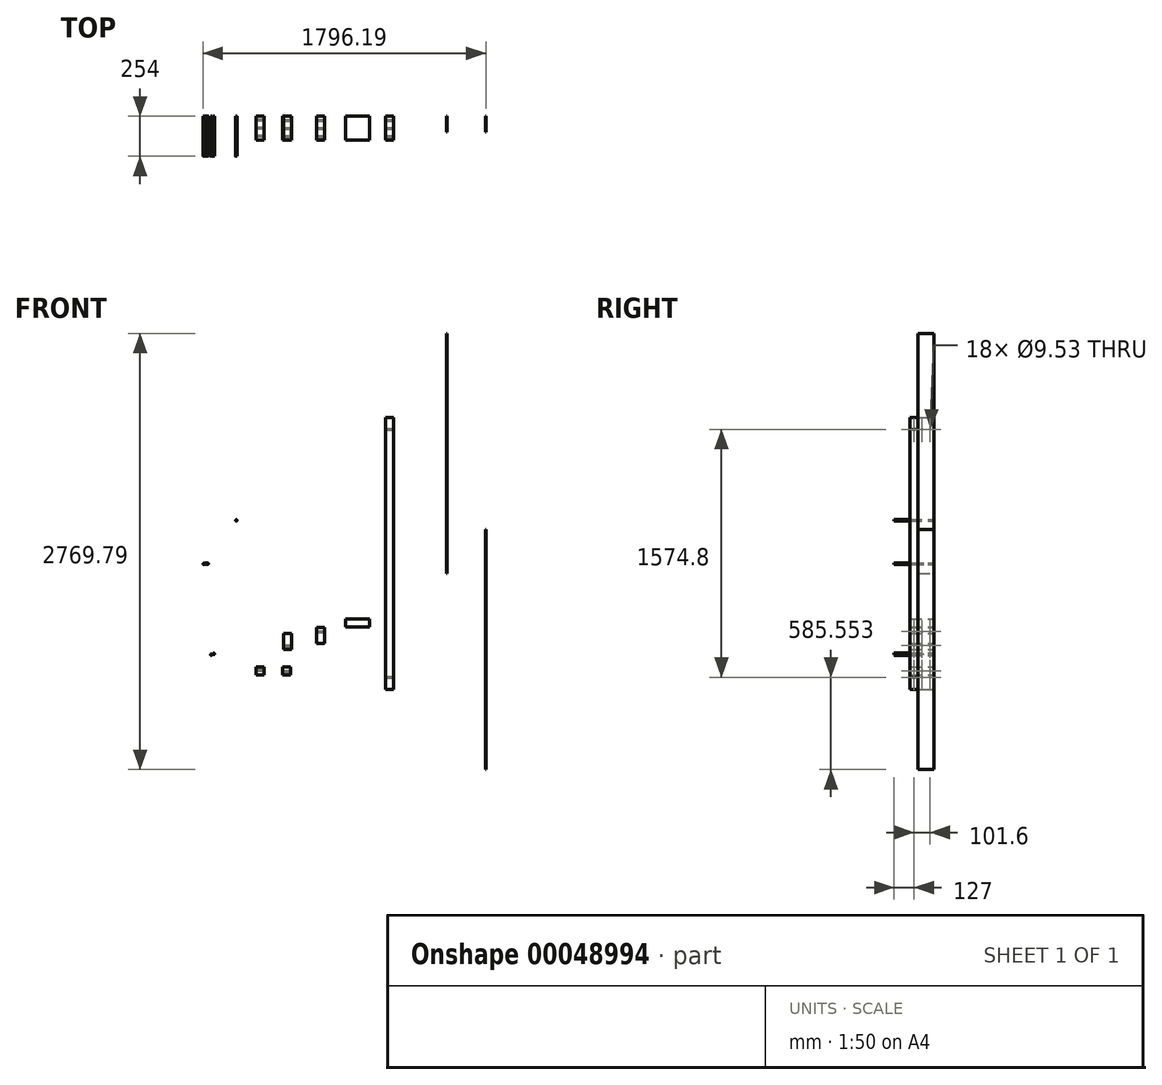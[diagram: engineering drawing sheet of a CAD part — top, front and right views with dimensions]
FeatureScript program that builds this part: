
annotation { "Feature Type Name" : "Feature", "Feature Type Description" : "" }
export const myFeature = defineFeature(function(context is Context, id is Id, definition is map)
    precondition{}
    {
        {
            var Q0;
            Q0=qCreatedBy(makeId("Front.planeOp"),FACE);
            var sketch = newSketch(context, id + "F0", { "sketchPlane" : qUnion([Q0])});
            skLineSegment(sketch, "E0.bottom", {"start": v(-472.01, 118.29) * mm, "end": v(-421.21, 118.29) * mm});
            skLineSegment(sketch, "E0.top", {"start": v(-472.01, 16.69) * mm, "end": v(-421.21, 16.69) * mm});
            skLineSegment(sketch, "E0.left", {"start": v(-472.01, 118.29) * mm, "end": v(-472.01, 16.69) * mm});
            skLineSegment(sketch, "E0.right", {"start": v(-421.21, 118.29) * mm, "end": v(-421.21, 16.69) * mm});
            skLineSegment(sketch, "E1.top", {"start": v(-262.5, 54) * mm, "end": v(-211.7, 54) * mm});
            skLineSegment(sketch, "E1.left", {"start": v(-262.5, 155.6) * mm, "end": v(-262.5, 54) * mm});
            skLineSegment(sketch, "E1.right", {"start": v(-211.7, 155.6) * mm, "end": v(-211.7, 54) * mm});
            skLineSegment(sketch, "E1.bottom", {"start": v(-262.5, 155.6) * mm, "end": v(-211.7, 155.6) * mm});
            skLineSegment(sketch, "E2.bottom", {"start": v(-645.87, -93.88) * mm, "end": v(-595.07, -93.88) * mm});
            skLineSegment(sketch, "E2.top", {"start": v(-645.87, -144.68) * mm, "end": v(-595.07, -144.68) * mm});
            skLineSegment(sketch, "E2.left", {"start": v(-645.87, -93.88) * mm, "end": v(-645.87, -144.68) * mm});
            skLineSegment(sketch, "E2.right", {"start": v(-595.07, -93.88) * mm, "end": v(-595.07, -144.68) * mm});
            skLineSegment(sketch, "E3.bottom", {"start": v(-479.26, -94.3) * mm, "end": v(-428.46, -94.3) * mm});
            skLineSegment(sketch, "E3.top", {"start": v(-479.26, -145.1) * mm, "end": v(-428.46, -145.1) * mm});
            skLineSegment(sketch, "E3.left", {"start": v(-479.26, -94.3) * mm, "end": v(-479.26, -145.1) * mm});
            skLineSegment(sketch, "E3.right", {"start": v(-428.46, -94.3) * mm, "end": v(-428.46, -145.1) * mm});
            skLineSegment(sketch, "E4.bottom", {"start": v(-77.8, 209.71) * mm, "end": v(74.6, 209.71) * mm});
            skLineSegment(sketch, "E4.top", {"start": v(-77.8, 158.91) * mm, "end": v(74.6, 158.91) * mm});
            skLineSegment(sketch, "E4.left", {"start": v(-77.8, 209.71) * mm, "end": v(-77.8, 158.91) * mm});
            skLineSegment(sketch, "E4.right", {"start": v(74.6, 209.71) * mm, "end": v(74.6, 158.91) * mm});
            skLineSegment(sketch, "E5.bottom", {"start": v(177.1, 1490.91) * mm, "end": v(227.9, 1490.91) * mm});
            skLineSegment(sketch, "E5.top", {"start": v(177.1, -236.29) * mm, "end": v(227.9, -236.29) * mm});
            skLineSegment(sketch, "E5.left", {"start": v(177.1, 1490.91) * mm, "end": v(177.1, -236.29) * mm});
            skLineSegment(sketch, "E5.right", {"start": v(227.9, 1490.91) * mm, "end": v(227.9, -236.29) * mm});
            skSolve(sketch);
        }
        {
            var Q0;
            Q0=makeQuery(id+"F0.imprint","IMPRINT",FACE,{"disambiguationData":[TD([[makeQuery(id+"F0.imprint","IMPRINT",EDGE,{"derivedFrom":sQuery(id+"F0.wireOp",EDGE,"E0.bottom")}),-1.0]])]});
            extrude(context, id + "F1", {"entities" : qUnion([Q0]), "depth" : 152.4 * mm});
        }
        {
            var Q0;
            Q0=makeQuery(id+"F0.imprint","IMPRINT",FACE,{"disambiguationData":[TD([[makeQuery(id+"F0.imprint","IMPRINT",EDGE,{"derivedFrom":sQuery(id+"F0.wireOp",EDGE,"E1.top")}),1.0]])]});
            extrude(context, id + "F2", {"entities" : qUnion([Q0]), "depth" : 152.4 * mm});
        }
        {
            var Q0;
            Q0=makeQuery(id+"F0.imprint","IMPRINT",FACE,{"disambiguationData":[TD([[makeQuery(id+"F0.imprint","IMPRINT",EDGE,{"derivedFrom":sQuery(id+"F0.wireOp",EDGE,"E4.bottom")}),-1.0]])]});
            extrude(context, id + "F3", {"entities" : qUnion([Q0]), "depth" : 152.4 * mm});
        }
        {
            var Q0;
            Q0=makeQuery(id+"F0.imprint","IMPRINT",FACE,{"disambiguationData":[TD([[makeQuery(id+"F0.imprint","IMPRINT",EDGE,{"derivedFrom":sQuery(id+"F0.wireOp",EDGE,"E2.bottom")}),-1.0]])]});
            var Q1;
            Q1=makeQuery(id+"F0.imprint","IMPRINT",FACE,{"disambiguationData":[TD([[makeQuery(id+"F0.imprint","IMPRINT",EDGE,{"derivedFrom":sQuery(id+"F0.wireOp",EDGE,"E3.bottom")}),-1.0]])]});
            var Q2;
            Q2=makeQuery(id+"F0.imprint","IMPRINT",FACE,{"disambiguationData":[TD([[makeQuery(id+"F0.imprint","IMPRINT",EDGE,{"derivedFrom":sQuery(id+"F0.wireOp",EDGE,"E5.bottom")}),-1.0]])]});
            extrude(context, id + "F4", {"entities" : qUnion([Q0, Q1, Q2]), "depth" : 152.4 * mm});
        }
        {
            var Q0;
            Q0=qCreatedBy(makeId("Front.planeOp"),FACE);
            var sketch = newSketch(context, id + "F5", { "sketchPlane" : qUnion([Q0])});
            skLineSegment(sketch, "E6.bottom", {"start": v(563.4, 2024.15) * mm, "end": v(566.58, 2024.15) * mm});
            skLineSegment(sketch, "E6.top", {"start": v(563.4, 500.15) * mm, "end": v(566.58, 500.15) * mm});
            skLineSegment(sketch, "E6.left", {"start": v(563.4, 2024.15) * mm, "end": v(563.4, 500.15) * mm});
            skLineSegment(sketch, "E6.right", {"start": v(566.58, 2024.15) * mm, "end": v(566.58, 500.15) * mm});
            skLineSegment(sketch, "E7.right", {"start": v(813.62, 778.36) * mm, "end": v(813.62, -745.64) * mm});
            skLineSegment(sketch, "E7.left", {"start": v(810.45, 778.36) * mm, "end": v(810.45, -745.64) * mm});
            skLineSegment(sketch, "E7.top", {"start": v(810.45, -745.64) * mm, "end": v(813.62, -745.64) * mm});
            skLineSegment(sketch, "E7.bottom", {"start": v(810.45, 778.36) * mm, "end": v(813.62, 778.36) * mm});
            skSolve(sketch);
        }
        {
            var Q0;
            Q0=makeQuery(id+"F5.imprint","IMPRINT",FACE,{"disambiguationData":[TD([[makeQuery(id+"F5.imprint","IMPRINT",EDGE,{"derivedFrom":sQuery(id+"F5.wireOp",EDGE,"E6.bottom")}),-1.0]])]});
            var Q1;
            Q1=makeQuery(id+"F5.imprint","IMPRINT",FACE,{"disambiguationData":[TD([[makeQuery(id+"F5.imprint","IMPRINT",EDGE,{"derivedFrom":sQuery(id+"F5.wireOp",EDGE,"E7.right")}),-1.0]])]});
            extrude(context, id + "F6", {"entities" : qUnion([Q0, Q1]), "depth" : 101.6 * mm});
        }
        {
            var Q0;
            Q0=qCreatedBy(makeId("Front.planeOp"),FACE);
            var sketch = newSketch(context, id + "F7", { "sketchPlane" : qUnion([Q0])});
            skCircle(sketch, "E8", {"center": v(-772.5, 836.22) * mm, "radius": 4.76 * mm});
            skSolve(sketch);
        }
        {
            var Q0;
            Q0=makeQuery(id+"F7.imprint","IMPRINT",FACE,{"disambiguationData":[TD([[makeQuery(id+"F7.imprint","IMPRINT",EDGE,{"derivedFrom":sQuery(id+"F7.wireOp",EDGE,"E8")}),1.0]])]});
            extrude(context, id + "F8", {"entities" : qUnion([Q0]), "depth" : 254 * mm});
        }
        {
            var Q0;
            Q0=qCreatedBy(makeId("Front.planeOp"),FACE);
            var sketch = newSketch(context, id + "F9", { "sketchPlane" : qUnion([Q0])});
            skCircle(sketch, "E9", {"center": v(-931.08, -16.23) * mm, "radius": 4.76 * mm});
            skSolve(sketch);
        }
        {
            var Q0;
            Q0=qCreatedBy(makeId("Front.planeOp"),FACE);
            var sketch = newSketch(context, id + "F10", { "sketchPlane" : qUnion([Q0])});
            skCircle(sketch, "E10", {"center": v(-915.13, -11.65) * mm, "radius": 4.76 * mm});
            skSolve(sketch);
        }
        {
            var Q0;
            Q0=makeQuery(id+"F9.imprint","IMPRINT",FACE,{"disambiguationData":[TD([[makeQuery(id+"F9.imprint","IMPRINT",EDGE,{"derivedFrom":sQuery(id+"F9.wireOp",EDGE,"E9")}),1.0]])]});
            var Q1;
            Q1=makeQuery(id+"F10.imprint","IMPRINT",FACE,{"disambiguationData":[TD([[makeQuery(id+"F10.imprint","IMPRINT",EDGE,{"derivedFrom":sQuery(id+"F10.wireOp",EDGE,"E10")}),1.0]])]});
            extrude(context, id + "F11", {"entities" : qUnion([Q0, Q1]), "depth" : 254 * mm});
        }
        {
            var Q0;
            Q0=makeQuery(id+"F4.opExtrude","SWEPT_FACE",FACE,{"disambiguationData":[OSD([sQuery(id+"F0.wireOp",EDGE,"E2.left")])]});
            var sketch = newSketch(context, id + "F12", { "sketchPlane" : qUnion([Q0])});
            skLineSegment(sketch, "E11.bottom", {"start": v(152.4, -93.88) * mm, "end": v(127, -93.88) * mm});
            skLineSegment(sketch, "E11.top", {"start": v(152.4, -119.28) * mm, "end": v(127, -119.28) * mm});
            skLineSegment(sketch, "E11.left", {"start": v(152.4, -93.88) * mm, "end": v(152.4, -119.28) * mm});
            skLineSegment(sketch, "E11.right", {"start": v(127, -93.88) * mm, "end": v(127, -119.28) * mm});
            skLineSegment(sketch, "E12.bottom", {"start": v(0, -93.88) * mm, "end": v(25.4, -93.88) * mm});
            skLineSegment(sketch, "E12.top", {"start": v(0, -119.28) * mm, "end": v(25.4, -119.28) * mm});
            skLineSegment(sketch, "E12.left", {"start": v(0, -93.88) * mm, "end": v(0, -119.28) * mm});
            skLineSegment(sketch, "E12.right", {"start": v(25.4, -93.88) * mm, "end": v(25.4, -119.28) * mm});
            skLineSegment(sketch, "E13.bottom", {"start": v(0, -93.88) * mm, "end": v(76.2, -93.88) * mm});
            skLineSegment(sketch, "E13.top", {"start": v(0, -119.28) * mm, "end": v(76.2, -119.28) * mm});
            skLineSegment(sketch, "E13.right", {"start": v(76.2, -93.88) * mm, "end": v(76.2, -119.28) * mm});
            skSolve(sketch);
        }
        {
            var Q0;
            Q0=sQuery(id+"F12.wireOp",VERTEX,"E12.top.end");
            var Q1;
            Q1=sQuery(id+"F12.wireOp",VERTEX,"E11.right.end");
            var Q2;
            Q2=sQuery(id+"F12.wireOp",VERTEX,"E13.top.end");
            var Q3;
            Q3=makeQuery(id+"F4.opExtrude","SWEPT_BODY",BODY,{"disambiguationData":[OSD([sQuery(id+"F0.wireOp",EDGE,"E2.bottom"),sQuery(id+"F0.wireOp",EDGE,"E2.top"),sQuery(id+"F0.wireOp",EDGE,"E2.left"),sQuery(id+"F0.wireOp",EDGE,"E2.right")])]});
            hole(context, id + "F13", {"style" : HoleStyle.SIMPLE, "holeDiameter" : 9.52 * mm, "endStyle" : HoleEndStyle.THROUGH, "locations" : qUnion([Q0, Q1, Q2]), "scope" : qUnion([Q3])});
        }
        {
            var Q0;
            Q0=makeQuery(id+"F4.opExtrude","SWEPT_FACE",FACE,{"disambiguationData":[OSD([sQuery(id+"F0.wireOp",EDGE,"E3.right")])]});
            var sketch = newSketch(context, id + "F14", { "sketchPlane" : qUnion([Q0])});
            skLineSegment(sketch, "E14.bottom", {"start": v(-152.4, -94.3) * mm, "end": v(-127, -94.3) * mm});
            skLineSegment(sketch, "E14.top", {"start": v(-152.4, -119.7) * mm, "end": v(-127, -119.7) * mm});
            skLineSegment(sketch, "E14.left", {"start": v(-152.4, -94.3) * mm, "end": v(-152.4, -119.7) * mm});
            skLineSegment(sketch, "E14.right", {"start": v(-127, -94.3) * mm, "end": v(-127, -119.7) * mm});
            skLineSegment(sketch, "E15.bottom", {"start": v(0, -94.3) * mm, "end": v(-25.4, -94.3) * mm});
            skLineSegment(sketch, "E15.top", {"start": v(0, -119.7) * mm, "end": v(-25.4, -119.7) * mm});
            skLineSegment(sketch, "E15.left", {"start": v(0, -94.3) * mm, "end": v(0, -119.7) * mm});
            skLineSegment(sketch, "E15.right", {"start": v(-25.4, -94.3) * mm, "end": v(-25.4, -119.7) * mm});
            skLineSegment(sketch, "E16.bottom", {"start": v(0, -145.1) * mm, "end": v(-76.2, -145.1) * mm});
            skLineSegment(sketch, "E16.top", {"start": v(0, -119.7) * mm, "end": v(-76.2, -119.7) * mm});
            skLineSegment(sketch, "E16.left", {"start": v(0, -145.1) * mm, "end": v(0, -119.7) * mm});
            skLineSegment(sketch, "E16.right", {"start": v(-76.2, -145.1) * mm, "end": v(-76.2, -119.7) * mm});
            skSolve(sketch);
        }
        {
            var Q0;
            Q0=sQuery(id+"F14.wireOp",VERTEX,"E14.top.end");
            var Q1;
            Q1=sQuery(id+"F14.wireOp",VERTEX,"E16.right.end");
            var Q2;
            Q2=sQuery(id+"F14.wireOp",VERTEX,"E15.right.end");
            var Q3;
            Q3=makeQuery(id+"F4.opExtrude","SWEPT_BODY",BODY,{"disambiguationData":[OSD([sQuery(id+"F0.wireOp",EDGE,"E3.bottom"),sQuery(id+"F0.wireOp",EDGE,"E3.top"),sQuery(id+"F0.wireOp",EDGE,"E3.left"),sQuery(id+"F0.wireOp",EDGE,"E3.right")])]});
            hole(context, id + "F15", {"style" : HoleStyle.SIMPLE, "holeDiameter" : 9.52 * mm, "endStyle" : HoleEndStyle.THROUGH, "locations" : qUnion([Q0, Q1, Q2]), "scope" : qUnion([Q3])});
        }
        {
            var Q0;
            Q0=makeQuery(id+"F1.opExtrude","SWEPT_FACE",FACE,{"disambiguationData":[OSD([sQuery(id+"F0.wireOp",EDGE,"E0.right")])]});
            var sketch = newSketch(context, id + "F16", { "sketchPlane" : qUnion([Q0])});
            skLineSegment(sketch, "E17.bottom", {"start": v(-152.4, 16.69) * mm, "end": v(-127, 16.69) * mm});
            skLineSegment(sketch, "E17.top", {"start": v(-152.4, 42.09) * mm, "end": v(-127, 42.09) * mm});
            skLineSegment(sketch, "E17.left", {"start": v(-152.4, 16.69) * mm, "end": v(-152.4, 42.09) * mm});
            skLineSegment(sketch, "E17.right", {"start": v(-127, 16.69) * mm, "end": v(-127, 42.09) * mm});
            skLineSegment(sketch, "E18.bottom", {"start": v(0, 16.69) * mm, "end": v(-25.4, 16.69) * mm});
            skLineSegment(sketch, "E18.top", {"start": v(0, 42.09) * mm, "end": v(-25.4, 42.09) * mm});
            skLineSegment(sketch, "E18.left", {"start": v(0, 16.69) * mm, "end": v(0, 42.09) * mm});
            skLineSegment(sketch, "E18.right", {"start": v(-25.4, 16.69) * mm, "end": v(-25.4, 42.09) * mm});
            skLineSegment(sketch, "E19.bottom", {"start": v(0, 16.69) * mm, "end": v(-76.2, 16.69) * mm});
            skLineSegment(sketch, "E19.top", {"start": v(0, 42.09) * mm, "end": v(-76.2, 42.09) * mm});
            skLineSegment(sketch, "E19.right", {"start": v(-76.2, 16.69) * mm, "end": v(-76.2, 42.09) * mm});
            skSolve(sketch);
        }
        {
            var Q0;
            Q0=sQuery(id+"F16.wireOp",VERTEX,"E17.right.end");
            var Q1;
            Q1=sQuery(id+"F16.wireOp",VERTEX,"E19.top.end");
            var Q2;
            Q2=sQuery(id+"F16.wireOp",VERTEX,"E18.right.end");
            var Q3;
            Q3=makeQuery(id+"F1.opExtrude","SWEPT_BODY",BODY,{"disambiguationData":[OSD([sQuery(id+"F0.wireOp",EDGE,"E0.bottom"),sQuery(id+"F0.wireOp",EDGE,"E0.top"),sQuery(id+"F0.wireOp",EDGE,"E0.left"),sQuery(id+"F0.wireOp",EDGE,"E0.right")])]});
            hole(context, id + "F17", {"style" : HoleStyle.SIMPLE, "holeDiameter" : 9.52 * mm, "endStyle" : HoleEndStyle.THROUGH, "locations" : qUnion([Q0, Q1, Q2]), "scope" : qUnion([Q3])});
        }
        {
            var Q0;
            Q0=makeQuery(id+"F2.opExtrude","SWEPT_FACE",FACE,{"disambiguationData":[OSD([sQuery(id+"F0.wireOp",EDGE,"E1.right")])]});
            var sketch = newSketch(context, id + "F18", { "sketchPlane" : qUnion([Q0])});
            skLineSegment(sketch, "E20.bottom", {"start": v(-152.4, 54) * mm, "end": v(-127, 54) * mm});
            skLineSegment(sketch, "E20.top", {"start": v(-152.4, 130.2) * mm, "end": v(-127, 130.2) * mm});
            skLineSegment(sketch, "E20.left", {"start": v(-152.4, 54) * mm, "end": v(-152.4, 130.2) * mm});
            skLineSegment(sketch, "E20.right", {"start": v(-127, 54) * mm, "end": v(-127, 130.2) * mm});
            skLineSegment(sketch, "E21.bottom", {"start": v(-152.4, 54) * mm, "end": v(-76.2, 54) * mm});
            skLineSegment(sketch, "E21.top", {"start": v(-152.4, 130.2) * mm, "end": v(-76.2, 130.2) * mm});
            skLineSegment(sketch, "E21.right", {"start": v(-76.2, 54) * mm, "end": v(-76.2, 130.2) * mm});
            skLineSegment(sketch, "E22.bottom", {"start": v(0, 54) * mm, "end": v(-25.4, 54) * mm});
            skLineSegment(sketch, "E22.top", {"start": v(0, 130.2) * mm, "end": v(-25.4, 130.2) * mm});
            skLineSegment(sketch, "E22.left", {"start": v(0, 54) * mm, "end": v(0, 130.2) * mm});
            skLineSegment(sketch, "E22.right", {"start": v(-25.4, 54) * mm, "end": v(-25.4, 130.2) * mm});
            skSolve(sketch);
        }
        {
            var Q0;
            Q0=sQuery(id+"F18.wireOp",VERTEX,"E20.right.end");
            var Q1;
            Q1=sQuery(id+"F18.wireOp",VERTEX,"E21.top.end");
            var Q2;
            Q2=sQuery(id+"F18.wireOp",VERTEX,"E22.right.end");
            var Q3;
            Q3=makeQuery(id+"F2.opExtrude","SWEPT_BODY",BODY,{"disambiguationData":[OSD([sQuery(id+"F0.wireOp",EDGE,"E1.top"),sQuery(id+"F0.wireOp",EDGE,"E1.left"),sQuery(id+"F0.wireOp",EDGE,"E1.right"),sQuery(id+"F0.wireOp",EDGE,"E1.bottom")])]});
            hole(context, id + "F19", {"style" : HoleStyle.SIMPLE, "holeDiameter" : 9.52 * mm, "endStyle" : HoleEndStyle.THROUGH, "locations" : qUnion([Q0, Q1, Q2]), "scope" : qUnion([Q3])});
        }
        {
            var Q0;
            Q0=makeQuery(id+"F4.opExtrude","SWEPT_FACE",FACE,{"disambiguationData":[OSD([sQuery(id+"F0.wireOp",EDGE,"E5.right")])]});
            var sketch = newSketch(context, id + "F20", { "sketchPlane" : qUnion([Q0])});
            skLineSegment(sketch, "E23.bottom", {"start": v(-152.4, 1490.91) * mm, "end": v(-127, 1490.91) * mm});
            skLineSegment(sketch, "E23.top", {"start": v(-152.4, 1414.71) * mm, "end": v(-127, 1414.71) * mm});
            skLineSegment(sketch, "E23.left", {"start": v(-152.4, 1490.91) * mm, "end": v(-152.4, 1414.71) * mm});
            skLineSegment(sketch, "E23.right", {"start": v(-127, 1490.91) * mm, "end": v(-127, 1414.71) * mm});
            skLineSegment(sketch, "E24.bottom", {"start": v(-152.4, 1490.91) * mm, "end": v(-76.2, 1490.91) * mm});
            skLineSegment(sketch, "E24.top", {"start": v(-152.4, 1414.71) * mm, "end": v(-76.2, 1414.71) * mm});
            skLineSegment(sketch, "E24.right", {"start": v(-76.2, 1490.91) * mm, "end": v(-76.2, 1414.71) * mm});
            skLineSegment(sketch, "E25.bottom", {"start": v(0, 1490.91) * mm, "end": v(-25.4, 1490.91) * mm});
            skLineSegment(sketch, "E25.top", {"start": v(0, 1414.71) * mm, "end": v(-25.4, 1414.71) * mm});
            skLineSegment(sketch, "E25.left", {"start": v(0, 1490.91) * mm, "end": v(0, 1414.71) * mm});
            skLineSegment(sketch, "E25.right", {"start": v(-25.4, 1490.91) * mm, "end": v(-25.4, 1414.71) * mm});
            skLineSegment(sketch, "E26.bottom", {"start": v(-152.4, -236.29) * mm, "end": v(-127, -236.29) * mm});
            skLineSegment(sketch, "E26.top", {"start": v(-152.4, -160.09) * mm, "end": v(-127, -160.09) * mm});
            skLineSegment(sketch, "E26.left", {"start": v(-152.4, -236.29) * mm, "end": v(-152.4, -160.09) * mm});
            skLineSegment(sketch, "E26.right", {"start": v(-127, -236.29) * mm, "end": v(-127, -160.09) * mm});
            skLineSegment(sketch, "E27.bottom", {"start": v(-152.4, -236.29) * mm, "end": v(-76.2, -236.29) * mm});
            skLineSegment(sketch, "E27.top", {"start": v(-152.4, -160.09) * mm, "end": v(-76.2, -160.09) * mm});
            skLineSegment(sketch, "E27.right", {"start": v(-76.2, -236.29) * mm, "end": v(-76.2, -160.09) * mm});
            skLineSegment(sketch, "E28.bottom", {"start": v(0, -236.29) * mm, "end": v(-25.4, -236.29) * mm});
            skLineSegment(sketch, "E28.top", {"start": v(0, -160.09) * mm, "end": v(-25.4, -160.09) * mm});
            skLineSegment(sketch, "E28.left", {"start": v(0, -236.29) * mm, "end": v(0, -160.09) * mm});
            skLineSegment(sketch, "E28.right", {"start": v(-25.4, -236.29) * mm, "end": v(-25.4, -160.09) * mm});
            skSolve(sketch);
        }
        {
            var Q0;
            Q0=sQuery(id+"F20.wireOp",VERTEX,"E26.top.end");
            var Q1;
            Q1=sQuery(id+"F20.wireOp",VERTEX,"E27.top.end");
            var Q2;
            Q2=sQuery(id+"F20.wireOp",VERTEX,"E28.top.end");
            var Q3;
            Q3=sQuery(id+"F20.wireOp",VERTEX,"E23.top.end");
            var Q4;
            Q4=sQuery(id+"F20.wireOp",VERTEX,"E24.top.end");
            var Q5;
            Q5=sQuery(id+"F20.wireOp",VERTEX,"E25.top.end");
            var Q6;
            Q6=makeQuery(id+"F4.opExtrude","SWEPT_BODY",BODY,{"disambiguationData":[OSD([sQuery(id+"F0.wireOp",EDGE,"E5.bottom"),sQuery(id+"F0.wireOp",EDGE,"E5.top"),sQuery(id+"F0.wireOp",EDGE,"E5.left"),sQuery(id+"F0.wireOp",EDGE,"E5.right")])]});
            hole(context, id + "F21", {"style" : HoleStyle.SIMPLE, "holeDiameter" : 9.52 * mm, "endStyle" : HoleEndStyle.THROUGH, "locations" : qUnion([Q0, Q1, Q2, Q3, Q4, Q5]), "scope" : qUnion([Q6])});
        }
        {
            var Q0;
            Q0=qCreatedBy(makeId("Front.planeOp"),FACE);
            var sketch = newSketch(context, id + "F22", { "sketchPlane" : qUnion([Q0])});
            skCircle(sketch, "E29", {"center": v(-977.8, 560.46) * mm, "radius": 4.76 * mm});
            skCircle(sketch, "E30", {"center": v(-965.07, 561.98) * mm, "radius": 4.76 * mm});
            skCircle(sketch, "E31", {"center": v(-953.46, 561.87) * mm, "radius": 4.76 * mm});
            skSolve(sketch);
        }
        {
            var Q0;
            Q0 = qSketchRegion(id + "F22", true);
            extrude(context, id + "F23", {"entities" : qUnion([Q0]), "depth" : 254 * mm});
        }
    });
